# Revit family: Угловой элемент КРК_КВК
name_source: partatom
category: Оборудование
units: mm (PartAtom-declared; Revit-internal decimal feet)

## family parameters
Всегда вертикально = Да
Классификация = Нет
На основе рабочей плоскости = Нет
Общий = Нет
При загрузке вырезать с полостями = Да
Размер круглого соединителя = Использовать диаметр
Тип детали = Нормальный
Точка расчета площади = Нет

## types (18) — shared parameters
ADSK_Наименование = Угловой элемент
ADSK_Обозначение = КРК/КВК
Высота = 81 мм

## per-type parameters (varying)
| type | B | b | Длина решетки | Конец решетки | Начало решетки | Смещение планки | Тип решетки | а |
| Угловой элемент B=201мм, a=90град | 201 мм | 240 мм | 239 мм | 80 мм | -119 мм | -120 мм | Решетка 90град B=201 | 90.00° |
| Угловой элемент B=201мм, a=120град | 201 мм | 154 мм | 153 мм | 37 мм | -76 мм | -77 мм | Решетка 120град B=201 | 120.00° |
| Угловой элемент B=201мм, a=135град | 201 мм | 121 мм | 120 мм | 21 мм | -60 мм | -61 мм | Решетка 135град B=201 | 135.00° |
| Угловой элемент B=241мм, a=90град | 241 мм | 280 мм | 279 мм | 100 мм | -139 мм | -140 мм | Решетка 90град B=241 | 90.00° |
| Угловой элемент B=241мм, a=120град | 241 мм | 177 мм | 176 мм | 49 мм | -88 мм | -89 мм | Решетка 120град B=241 | 120.00° |
| Угловой элемент B=241мм, a=135град | 241 мм | 138 мм | 137 мм | 29 мм | -68 мм | -69 мм | Решетка 135град B=241 | 135.00° |
| Угловой элемент B=271мм, a=90град | 271 мм | 310 мм | 309 мм | 115 мм | -154 мм | -155 мм | Решетка 90град B=271 | 90.00° |
| Угловой элемент B=271мм, a=120град | 271 мм | 194 мм | 193 мм | 57 мм | -96 мм | -97 мм | Решетка 120град B=271 | 120.00° |
| Угловой элемент B=271мм, a=135град | 271 мм | 150 мм | 149 мм | 35 мм | -74 мм | -75 мм | Решетка 135град B=271 | 135.00° |
| Угловой элемент B=341мм, a=90град | 341 мм | 380 мм | 379 мм | 150 мм | -189 мм | -190 мм | Решетка 90град B=341 | 90.00° |
| Угловой элемент B=371мм, a=135град | 371 мм | 192 мм | 191 мм | 56 мм | -95 мм | -96 мм | Решетка 135град B=371 | 135.00° |
| Угловой элемент B=371мм, a=90град | 371 мм | 410 мм | 409 мм | 165 мм | -204 мм | -205 мм | Решетка 90град B=371 | 90.00° |
| Угловой элемент B=431мм, a=90град | 431 мм | 470 мм | 469 мм | 195 мм | -234 мм | -235 мм | Решетка 90град B=431 | 90.00° |
| Угловой элемент B=431мм, a=120град | 431 мм | 329 мм | 328 мм | 125 мм | -164 мм | -165 мм | Решетка 120град B=431 | 120.00° |
| Угловой элемент B=431мм, a=135град | 431 мм | 216 мм | 215 мм | 68 мм | -107 мм | -108 мм | Решетка 135град B=431 | 135.00° |
| Угловой элемент B=341мм, a=120град | 341 мм | 235 мм | 234 мм | 78 мм | -117 мм | -118 мм | Решетка 120град B=341 | 120.00° |
| Угловой элемент B=341мм, a=135град | 341 мм | 180 мм | 179 мм | 50 мм | -89 мм | -90 мм | Решетка 135град B=341 | 135.00° |
| Угловой элемент B=371мм, a=120град | 371 мм | 252 мм | 251 мм | 86 мм | -125 мм | -126 мм | Решетка 120град B=371 | 120.00° |
